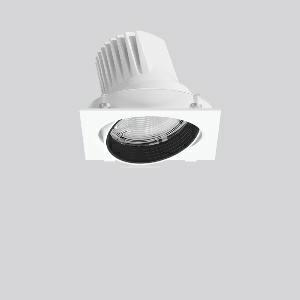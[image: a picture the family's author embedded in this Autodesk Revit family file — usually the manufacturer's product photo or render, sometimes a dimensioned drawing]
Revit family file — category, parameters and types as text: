
# Revit family: magcardo_maxi_722190_002_24ce
name_source: partatom
category: Lighting Fixtures
units: mm (PartAtom-declared; Revit-internal decimal feet)

## family parameters
Cut with Voids When Loaded = No
Host = Face
Light Source = No
Part Type = Normal
Room Calculation Point = No
Round Connector Dimension = Use Diameter
Shared = No

## types (1)
- MAGCARDO maxi (1 x LED Modul 930, 2850 lm, 3000)
    Apparent Load = 25 VA
    Approval mark = CE
    CIE Flux Codes = 97 100 100 100 100
    Color Rendering = 90
    Color Temperature = 3000
    Default Elevation = 1800 mm
    Description = Series: MAGCARDO maxi
Projector unit for tool-free mounting in separate recessed frame. Luminaire top: die-cast aluminium, powder-coated. Rotation range 356° and swivel range ± 35°. Inner cover prevents view into the false ceiling. Black plastic ring and recessed LED to prevent glare from the side. Optical assembly with lens made of plastic (polycarbonate) for the best homogeneous light distribution - can be changed without tools. Best colour rendering index Ra>90. Magnetic click locking mechanism for quick and convenient installation without tools: insert the recessed frame (1, 2 or 3-lamp) with clamp fastener (no tools required), push the luminaire head with the base plate into the recessed frame and fix magnetically. Including separate LED converter with connecting cable 600 mm.High quality converter without flickering and stroboscopic effect. Through-wiring box (5 pole) available as accessory. The following accessories can be mounted without use of tools: interchangeable lenses, honeycomb louvre, clear and frosted diffusers, white interchangeable plastic ring.Modular design: recessed mounting frame must be ordered separately! 
Colour: traffic white, matt (RAL 9016)
Length: 172 mm
Width: 167 mm
Height: 137 mm
Recess height: 155 mm
Lamp: LED
Socket: without socket
Colour temperature: 3000K
Colour rendering index (CRI): 92
System power: 25 W
Rated luminous flux: 2850 lm
Luminous efficiency: 114 lm/W
Control gear: Regulated power supply
Protection class: II
Type of protection: IP 20
    Height = 0 mm  [stored 0 ft]
    Lamp = 1 x LED Modul 930
    Lamp Light Flux = 2850 lm
    Lamp count = 1
    Length = 172 mm
    Lifetime = 50000 h
    Luminous efficacy = 114 lm/W
    Manufacturer = RZB
    ModVariant = No
    Model = 722190.002
    Mounting Place = Ceiling, Wall
    Mounting Type = Recessed
    Number of Poles = 1
    OnlyDefault = Yes
    Power Factor = 1
    Product Name = MAGCARDO maxi
    Product group = Recessed projectors
    ProductGroupID = 401
    Protection Class = Protection class II
    Protection Degree = IP 20
    RLX_Detail_Level = 1
    RLX_Emergency_Light_Flux = 0 lm
    RLX_Emergency_Type = 0
    RLX_Emergency_Type_DB = No
    RlxData = <blob elided: 40525 chars, md5=b941255b>
    Socket = socket
    Standby Power = 0 W
    System Light Flux = 2850 lm
    System Power = 25 W
    Type Comments = Product without accessories
    Type Image = 722048.002.jpg
    URL = http://relux.com
    VarID = ---
    Voltage = 230 V
    Voltage Range = 220-240 V
    Weight = 0.00 kg
    Width = 167 mm

note: [stored X ft] marks values corroborated as IEEE doubles in the binary element streams (Revit-internal decimal feet)

## geometry (parser evidence)
native form markers: Blend x4, Sweep x12
no freeform markers — native parametric forms only
